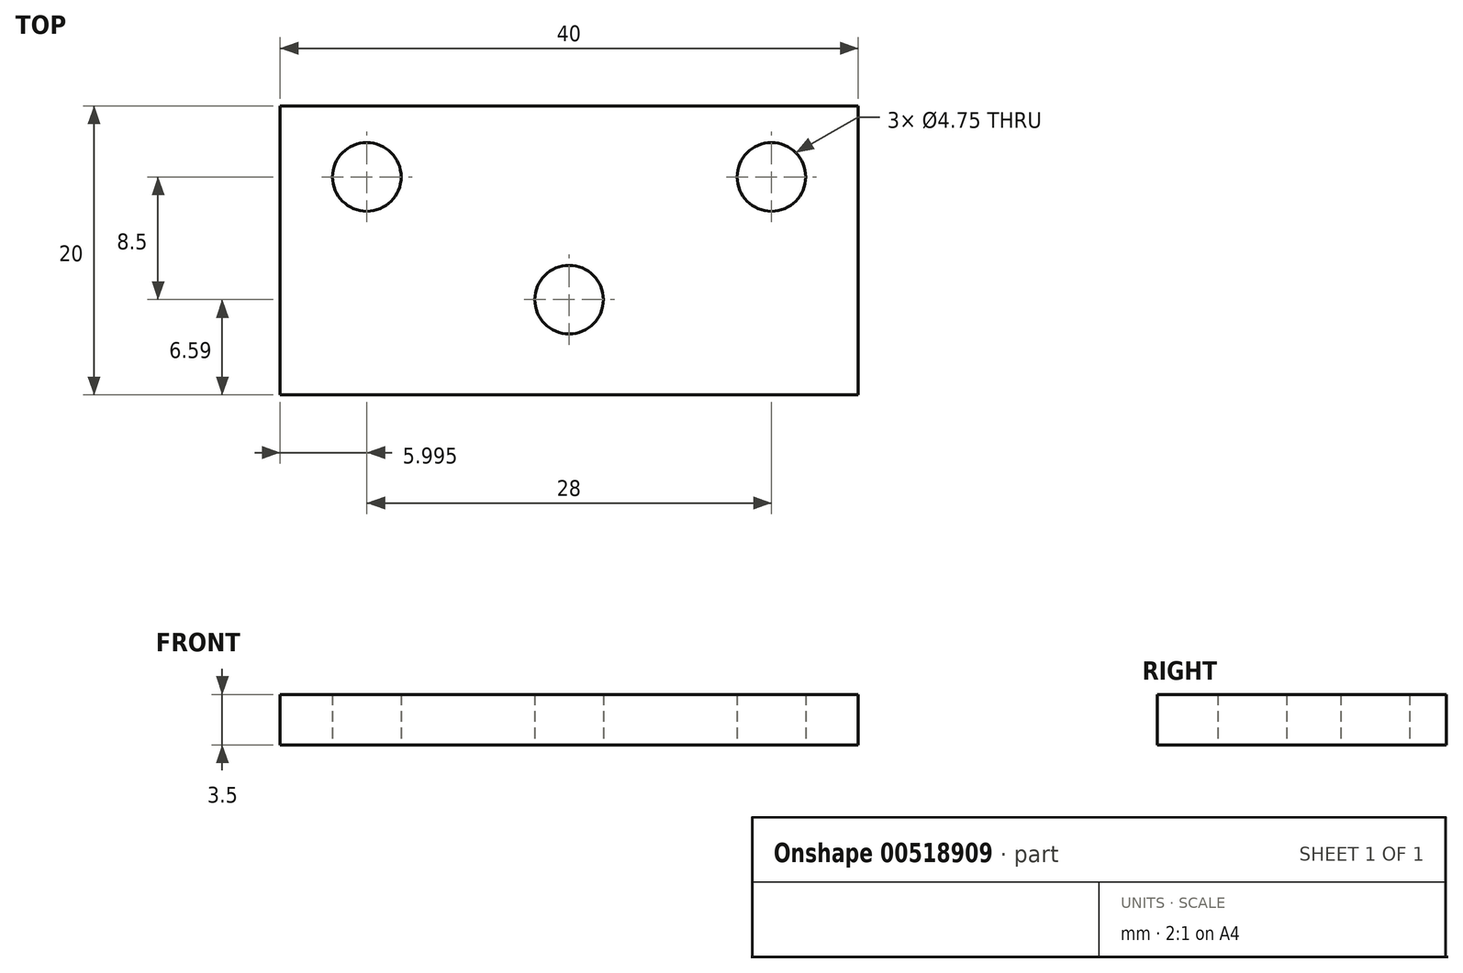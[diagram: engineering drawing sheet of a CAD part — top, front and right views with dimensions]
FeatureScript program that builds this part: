
annotation { "Feature Type Name" : "Feature", "Feature Type Description" : "" }
export const myFeature = defineFeature(function(context is Context, id is Id, definition is map)
    precondition{}
    {
        {
            var Q0;
            Q0=qCreatedBy(makeId("Top.planeOp"),FACE);
            var sketch = newSketch(context, id + "F0", { "sketchPlane" : qUnion([Q0])});
            skLineSegment(sketch, "E0.bottom", {"start": v(-17.72, 4.91) * mm, "end": v(22.28, 4.91) * mm});
            skLineSegment(sketch, "E0.top", {"start": v(-17.72, -15.09) * mm, "end": v(22.28, -15.09) * mm});
            skLineSegment(sketch, "E0.left", {"start": v(-17.72, 4.91) * mm, "end": v(-17.72, -15.09) * mm});
            skLineSegment(sketch, "E0.right", {"start": v(22.28, 4.91) * mm, "end": v(22.28, -15.09) * mm});
            skLineSegment(sketch, "E1", {"start": v(-17.72, 4.91) * mm, "end": v(22.28, -15.09) * mm, "construction": true});
            skLineSegment(sketch, "E2", {"start": v(22.28, 4.91) * mm, "end": v(-17.72, -15.09) * mm, "construction": true});
            skLineSegment(sketch, "E3", {"start": v(2.28, 4.91) * mm, "end": v(2.28, -15.09) * mm, "construction": true});
            skCircle(sketch, "E4", {"center": v(2.28, -8.5) * mm, "radius": 2.38 * mm});
            skCircle(sketch, "E5", {"center": v(-11.72, 0) * mm, "radius": 2.38 * mm});
            skCircle(sketch, "E6", {"center": v(16.28, 0) * mm, "radius": 2.38 * mm});
            skSolve(sketch);
        }
        {
            var Q0;
            Q0 = qSketchRegion(id + "F0", true);
            extrude(context, id + "F1", {"entities" : qUnion([Q0]), "depth" : 3.5 * mm, "offsetDistance" : 25 * mm});
        }
    });
